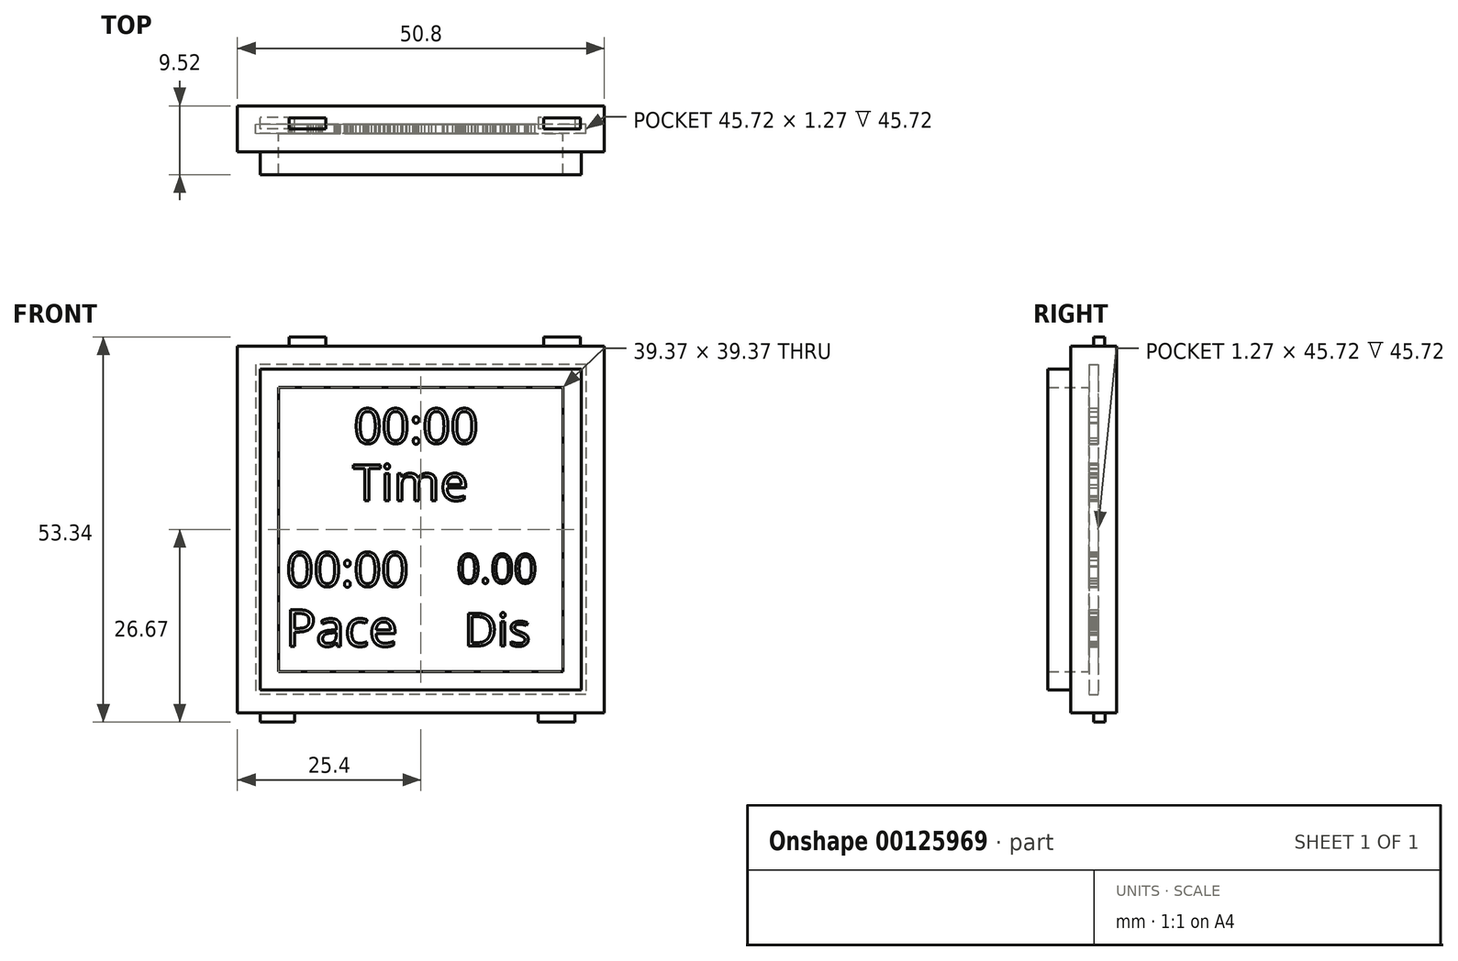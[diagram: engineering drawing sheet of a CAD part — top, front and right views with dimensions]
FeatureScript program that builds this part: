
annotation { "Feature Type Name" : "Feature", "Feature Type Description" : "" }
export const myFeature = defineFeature(function(context is Context, id is Id, definition is map)
    precondition{}
    {
        {
            var Q0;
            Q0=qCreatedBy(makeId("Front.planeOp"),FACE);
            var sketch = newSketch(context, id + "F0", { "sketchPlane" : qUnion([Q0])});
            skLineSegment(sketch, "E0.bottom", {"start": v(25.4, 25.4) * mm, "end": v(-25.4, 25.4) * mm});
            skLineSegment(sketch, "E0.top", {"start": v(25.4, -25.4) * mm, "end": v(-25.4, -25.4) * mm});
            skLineSegment(sketch, "E0.left", {"start": v(25.4, 25.4) * mm, "end": v(25.4, -25.4) * mm});
            skLineSegment(sketch, "E0.right", {"start": v(-25.4, 25.4) * mm, "end": v(-25.4, -25.4) * mm});
            skPoint(sketch, "E0.middle", {"position": v(0, 0) * mm});
            skSolve(sketch);
        }
        {
            var Q0;
            Q0 = qSketchRegion(id + "F0", true);
            extrude(context, id + "F1", {"entities" : qUnion([Q0]), "endBound" : BoundingType.SYMMETRIC, "depth" : 6.35 * mm});
        }
        {
            var Q0;
            Q0=makeQuery(id+"F1.opExtrude","CAP_FACE",FACE,{"disambiguationData":[OSD([sQuery(id+"F0.wireOp",EDGE,"E0.bottom"),sQuery(id+"F0.wireOp",EDGE,"E0.top"),sQuery(id+"F0.wireOp",EDGE,"E0.left"),sQuery(id+"F0.wireOp",EDGE,"E0.right")])],"isStart":false});
            var sketch = newSketch(context, id + "F2", { "sketchPlane" : qUnion([Q0])});
            skLineSegment(sketch, "E1.bottom", {"start": v(22.22, 22.23) * mm, "end": v(-22.23, 22.23) * mm});
            skLineSegment(sketch, "E1.top", {"start": v(22.23, -22.23) * mm, "end": v(-22.22, -22.23) * mm});
            skLineSegment(sketch, "E1.left", {"start": v(22.22, 22.23) * mm, "end": v(22.23, -22.23) * mm});
            skLineSegment(sketch, "E1.right", {"start": v(-22.23, 22.23) * mm, "end": v(-22.22, -22.23) * mm});
            skPoint(sketch, "E1.middle", {"position": v(0, 0) * mm});
            skSolve(sketch);
        }
        {
            var Q0;
            Q0=makeQuery(id+"F2.imprint","IMPRINT",FACE,{"disambiguationData":[TD([[makeQuery(id+"F2.imprint","IMPRINT",EDGE,{"derivedFrom":sQuery(id+"F2.wireOp",EDGE,"E1.bottom")}),1.0]])]});
            extrude(context, id + "F3", {"entities" : qUnion([Q0]), "operationType" : NewBodyOperationType.ADD, "endBound" : BoundingType.SYMMETRIC, "depth" : 6.35 * mm});
        }
        {
            var Q0;
            Q0=makeQuery(id+"F3.opExtrude","CAP_FACE",FACE,{"disambiguationData":[OSD([sQuery(id+"F2.wireOp",EDGE,"E1.bottom"),sQuery(id+"F2.wireOp",EDGE,"E1.top"),sQuery(id+"F2.wireOp",EDGE,"E1.left"),sQuery(id+"F2.wireOp",EDGE,"E1.right")])],"isStart":false});
            shell(context, id + "F4", {"entities" : qUnion([Q0]), "thickness" : 2.54 * mm});
        }
        {
            var Q0;
            {var subQ0=sQuery(id+"F0.wireOp",EDGE,"E0.right");var subQ1=sQuery(id+"F0.wireOp",EDGE,"E0.left");var subQ2=sQuery(id+"F0.wireOp",EDGE,"E0.top");var subQ3=sQuery(id+"F0.wireOp",EDGE,"E0.bottom");Q0=makeQuery(id+"F4.opShell","OFFSET_FACE",FACE,{"disambiguationData":[OSD([subQ3,subQ2,subQ1,subQ0]),TDD([makeQuery(id+"F1.opExtrude","CAP_FACE",FACE,{"disambiguationData":[OSD([subQ3,subQ2,subQ1,subQ0])],"isStart":true})])]});}
            var sketch = newSketch(context, id + "F5", { "sketchPlane" : qUnion([Q0])});
            skText(sketch, "E2", { "text": "00:00", "fontName": "OpenSans-Regular.ttf"});
            skText(sketch, "E3", { "text": "Time", "fontName": "OpenSans-Regular.ttf"});
            skText(sketch, "E4", { "text": "00:00", "fontName": "OpenSans-Regular.ttf"});
            skText(sketch, "E5", { "text": "Pace", "fontName": "OpenSans-Regular.ttf"});
            skText(sketch, "E6", { "text": "0.00", "fontName": "OpenSans-Regular.ttf"});
            skText(sketch, "E7", { "text": "Dis", "fontName": "OpenSans-Regular.ttf"});
            const initialGuessF5  = {"E2": [-0.0093, 0.01192, 1, 0, 0.00486], "E3": [-0.00941, 0.00402, 1, 0, 0.005], "E4": [-0.01866, -0.0079, 1, 0, 0.00478], "E5": [-0.01879, -0.01618, 1, 0, 0.0051], "E6": [0.00498, -0.00741, 1, 0, 0.00402], "E7": [0.00595, -0.01613, 1, 0, 0.00454]};
            skSetInitialGuess(sketch, initialGuessF5);
            skSolve(sketch);
        }
        {
            var Q0;
            Q0=makeQuery(id+"F1.opExtrude","SWEPT_FACE",FACE,{"disambiguationData":[OSD([sQuery(id+"F0.wireOp",EDGE,"E0.top")])]});
            var sketch = newSketch(context, id + "F6", { "sketchPlane" : qUnion([Q0])});
            skLineSegment(sketch, "E8.bottom", {"start": v(-22.28, -1.57) * mm, "end": v(-17.5, -1.57) * mm});
            skLineSegment(sketch, "E8.top", {"start": v(-22.28, 0) * mm, "end": v(-17.5, 0) * mm});
            skLineSegment(sketch, "E8.left", {"start": v(-22.28, -1.57) * mm, "end": v(-22.28, 0) * mm});
            skLineSegment(sketch, "E8.right", {"start": v(-17.5, -1.57) * mm, "end": v(-17.5, 0) * mm});
            skPoint(sketch, "E9.oppositeSnap0", {"position": v(-19.89, -1.57) * mm});
            skLineSegment(sketch, "E9.bottom", {"start": v(16.2, 0) * mm, "end": v(21.28, 0) * mm});
            skLineSegment(sketch, "E9.top", {"start": v(16.2, -1.57) * mm, "end": v(21.28, -1.57) * mm});
            skLineSegment(sketch, "E9.left", {"start": v(16.2, 0) * mm, "end": v(16.2, -1.57) * mm});
            skLineSegment(sketch, "E9.right", {"start": v(21.28, 0) * mm, "end": v(21.28, -1.57) * mm});
            skSolve(sketch);
        }
        {
            var Q0;
            Q0=makeQuery(id+"F1.opExtrude","SWEPT_FACE",FACE,{"disambiguationData":[OSD([sQuery(id+"F0.wireOp",EDGE,"E0.bottom")])]});
            var sketch = newSketch(context, id + "F7", { "sketchPlane" : qUnion([Q0])});
            skPoint(sketch, "E10.firstSnap0", {"position": v(25.4, 0) * mm});
            skLineSegment(sketch, "E10.bottom", {"start": v(22.08, 0) * mm, "end": v(17, 0) * mm});
            skLineSegment(sketch, "E10.top", {"start": v(22.08, 1.5) * mm, "end": v(17, 1.5) * mm});
            skLineSegment(sketch, "E10.left", {"start": v(22.08, 0) * mm, "end": v(22.08, 1.5) * mm});
            skLineSegment(sketch, "E10.right", {"start": v(17, 0) * mm, "end": v(17, 1.5) * mm});
            skLineSegment(sketch, "E11.bottom", {"start": v(-13.17, 0) * mm, "end": v(-18.25, 0) * mm});
            skLineSegment(sketch, "E11.top", {"start": v(-13.17, 1.48) * mm, "end": v(-18.25, 1.48) * mm});
            skLineSegment(sketch, "E11.left", {"start": v(-13.17, 0) * mm, "end": v(-13.17, 1.48) * mm});
            skLineSegment(sketch, "E11.right", {"start": v(-18.25, 0) * mm, "end": v(-18.25, 1.48) * mm});
            skSolve(sketch);
        }
        {
            var Q0;
            Q0 = qSketchRegion(id + "F5", true);
            extrude(context, id + "F8", {"entities" : qUnion([Q0]), "operationType" : NewBodyOperationType.ADD, "endBound" : BoundingType.SYMMETRIC, "depth" : 2.54 * mm});
        }
        {
            var Q0;
            Q0=makeQuery(id+"F6.imprint","IMPRINT",FACE,{"disambiguationData":[TD([[makeQuery(id+"F6.imprint","IMPRINT",EDGE,{"derivedFrom":sQuery(id+"F6.wireOp",EDGE,"E8.bottom")}),1.0]])]});
            var Q1;
            Q1=makeQuery(id+"F6.imprint","IMPRINT",FACE,{"disambiguationData":[TD([[makeQuery(id+"F6.imprint","IMPRINT",EDGE,{"derivedFrom":sQuery(id+"F6.wireOp",EDGE,"E9.bottom")}),-1.0]])]});
            extrude(context, id + "F9", {"entities" : qUnion([Q0, Q1]), "operationType" : NewBodyOperationType.ADD, "endBound" : BoundingType.SYMMETRIC, "depth" : 2.54 * mm});
        }
        {
            var Q0;
            Q0 = qSketchRegion(id + "F7", true);
            extrude(context, id + "F10", {"entities" : qUnion([Q0]), "operationType" : NewBodyOperationType.ADD, "endBound" : BoundingType.SYMMETRIC, "depth" : 2.54 * mm});
        }
    });
